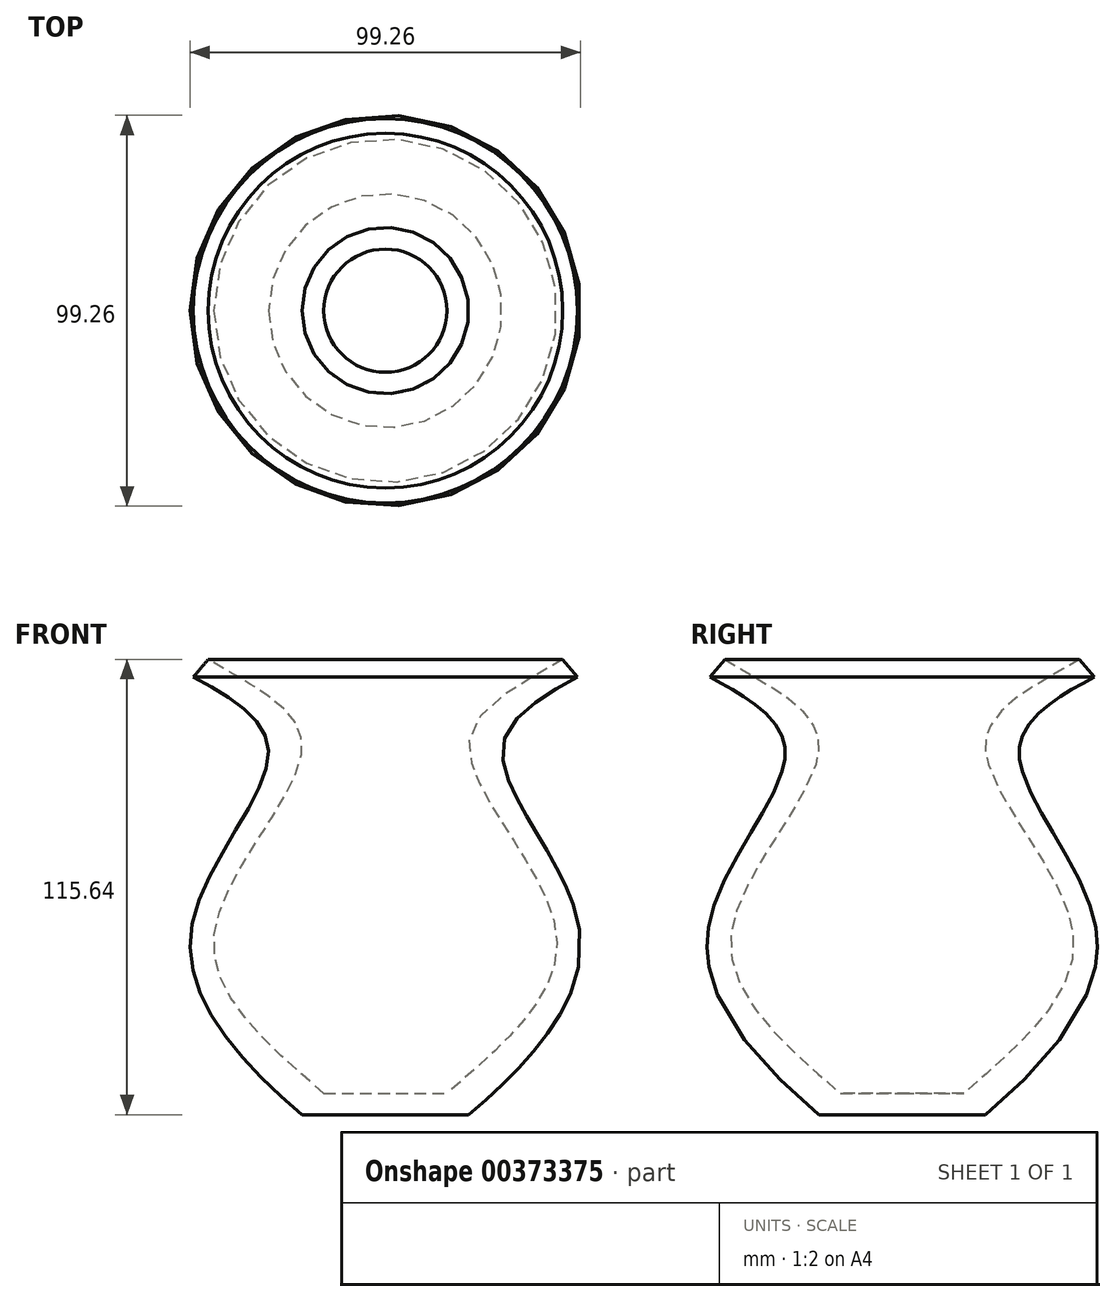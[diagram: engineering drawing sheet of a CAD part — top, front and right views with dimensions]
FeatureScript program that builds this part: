
annotation { "Feature Type Name" : "Feature", "Feature Type Description" : "" }
export const myFeature = defineFeature(function(context is Context, id is Id, definition is map)
    precondition{}
    {
        {
            var Q0;
            Q0=qCreatedBy(makeId("Front.planeOp"),FACE);
            var sketch = newSketch(context, id + "F0", { "sketchPlane" : qUnion([Q0])});
            skFitSpline(sketch, "E0", {"points": [v(-12.4, -46.26) * mm, v(15.88, 0) * mm, v(-3.85, 45.79) * mm, v(15.26, 64.9) * mm], "startDerivative": vector(122.81, 104.08) * mm, "endDerivative": vector(107.09, 57.85) * mm});
            skLineSegment(sketch, "E1", {"start": v(-33.55, -40.85) * mm, "end": v(-33.55, 74.87) * mm});
            skFitSpline(sketch, "E2", {"points": [v(-17.9, -40.85) * mm, v(9.85, 0) * mm, v(-12.4, 47.13) * mm, v(11.5, 69.38) * mm], "startDerivative": vector(127.42, 110.48) * mm, "endDerivative": vector(125.34, 74.2) * mm});
            skLineSegment(sketch, "E3", {"start": v(-17.9, -40.85) * mm, "end": v(-33.55, -40.85) * mm});
            skLineSegment(sketch, "E4", {"start": v(-12.4, -46.26) * mm, "end": v(-33.55, -46.26) * mm});
            skLineSegment(sketch, "E5", {"start": v(-33.55, -46.26) * mm, "end": v(-33.55, -40.85) * mm});
            skLineSegment(sketch, "E6", {"start": v(11.5, 69.38) * mm, "end": v(15.26, 64.9) * mm});
            skSolve(sketch);
        }
        {
            var Q0;
            Q0 = qSketchRegion(id + "F0", true);
            var Q1;
            Q1=sQuery(id+"F0.wireOp",EDGE,"E1");
            revolve(context, id + "F1", {"entities" : qUnion([Q0]), "axis" : qUnion([Q1]), "revolveType" : RevolveType.FULL});
        }
    });
